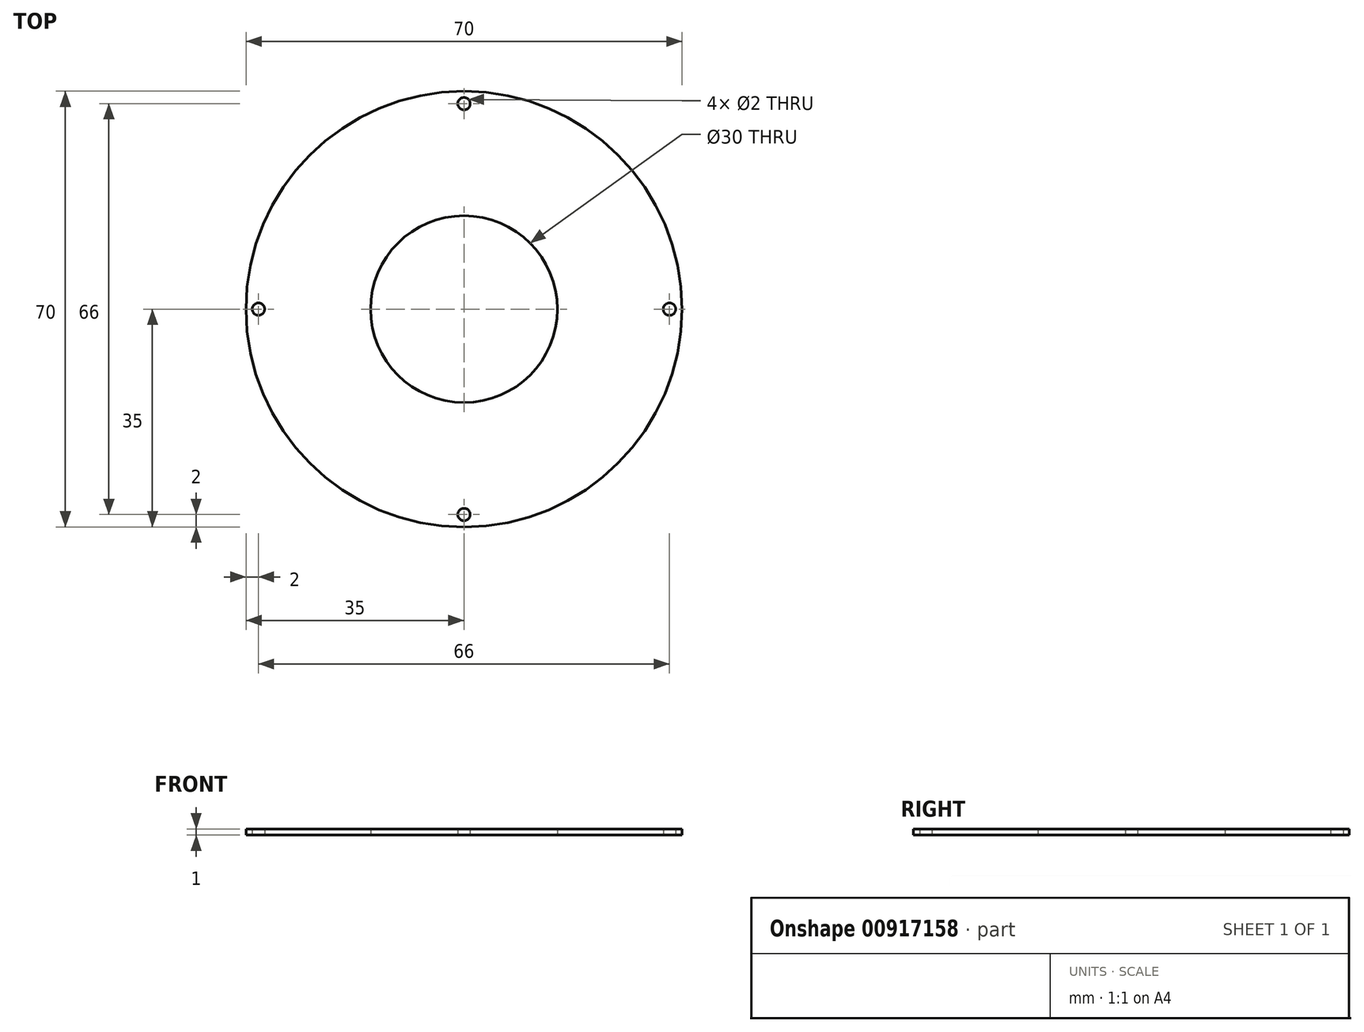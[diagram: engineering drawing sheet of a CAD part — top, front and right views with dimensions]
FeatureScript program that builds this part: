
annotation { "Feature Type Name" : "Feature", "Feature Type Description" : "" }
export const myFeature = defineFeature(function(context is Context, id is Id, definition is map)
    precondition{}
    {
        {
            var Q0;
            Q0=qCreatedBy(makeId("Top.planeOp"),FACE);
            var sketch = newSketch(context, id + "F0", { "sketchPlane" : qUnion([Q0])});
            skCircle(sketch, "E0", {"center": v(0, 0) * mm, "radius": 35 * mm});
            skCircle(sketch, "E1", {"center": v(0, 0) * mm, "radius": 15 * mm});
            skCircle(sketch, "E2", {"center": v(0, 33) * mm, "radius": 1 * mm});
            skCircle(sketch, "E3.1.0", {"center": v(-33, 0) * mm, "radius": 1 * mm});
            skCircle(sketch, "E3.2.0", {"center": v(0, -33) * mm, "radius": 1 * mm});
            skCircle(sketch, "E3.3.0", {"center": v(33, 0) * mm, "radius": 1 * mm});
            skSolve(sketch);
        }
        {
            var Q0;
            Q0 = qSketchRegion(id + "F0", true);
            extrude(context, id + "F1", {"entities" : qUnion([Q0]), "depth" : 1 * mm, "offsetDistance" : 25 * mm});
        }
    });
